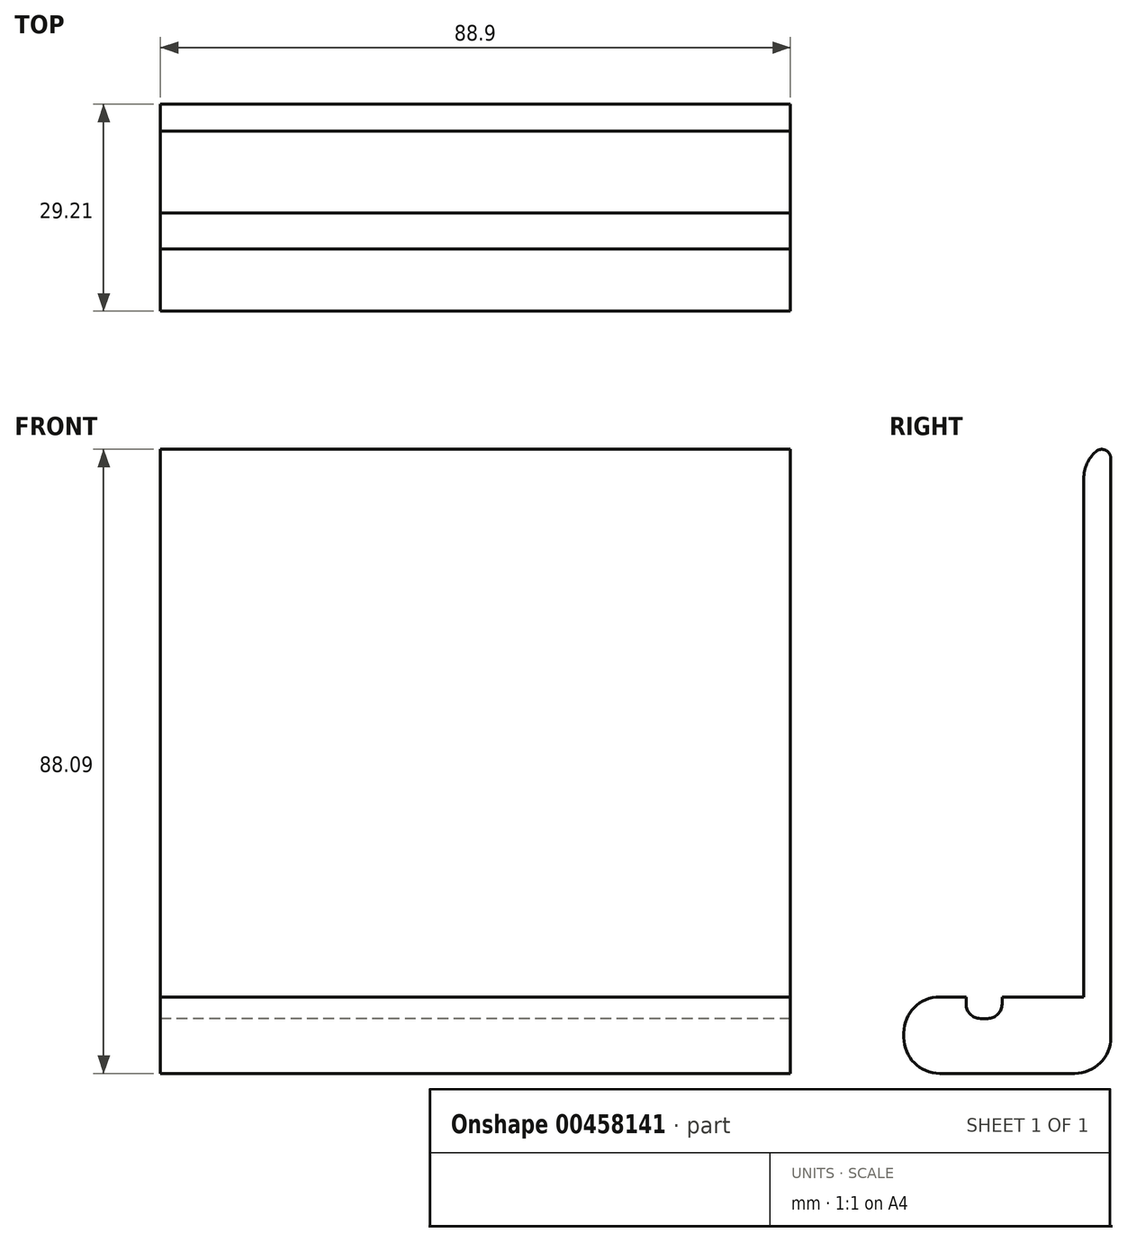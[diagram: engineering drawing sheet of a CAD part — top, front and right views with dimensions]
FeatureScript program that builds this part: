
annotation { "Feature Type Name" : "Feature", "Feature Type Description" : "" }
export const myFeature = defineFeature(function(context is Context, id is Id, definition is map)
    precondition{}
    {
        {
            var Q0;
            Q0=qCreatedBy(makeId("Front.planeOp"),FACE);
            var sketch = newSketch(context, id + "F0", { "sketchPlane" : qUnion([Q0])});
            skLineSegment(sketch, "E0", {"start": v(-36.8, -48.23) * mm, "end": v(52.1, -48.23) * mm});
            skLineSegment(sketch, "E1", {"start": v(-36.8, -48.23) * mm, "end": v(-36.8, 66.07) * mm});
            skLineSegment(sketch, "E2", {"start": v(52.1, -48.23) * mm, "end": v(52.1, 66.07) * mm});
            skLineSegment(sketch, "E3", {"start": v(-36.8, -37.43) * mm, "end": v(52.1, -37.43) * mm});
            skLineSegment(sketch, "E4", {"start": v(52.1, 66.07) * mm, "end": v(-36.8, 66.07) * mm});
            skSolve(sketch);
        }
        {
            var Q0;
            {var subQ0=sQuery(id+"F0.wireOp",EDGE,"vnEuTptI-VBLG-qhPj-jRMl-XnknEwSORpZn");Q0=makeQuery(id+"F0.imprint","IMPRINT",FACE,{"disambiguationData":[TD([[makeQuery(id+"F0.imprint","IMPRINT",EDGE,{"derivedFrom":subQ0}),1.0]])]});}
            var Q1;
            {var subQ0=sQuery(id+"F0.wireOp",EDGE,"xnTbnupX-NSSj-kjbL-TlVA-3KyHgeqRF7kW");Q1=makeQuery(id+"F0.imprint","IMPRINT",FACE,{"disambiguationData":[TD([[makeQuery(id+"F0.imprint","IMPRINT",EDGE,{"derivedFrom":subQ0}),1.0]])]});}
            var Q2;
            {var subQ0=sQuery(id+"F0.wireOp",EDGE,"E0");Q2=makeQuery(id+"F0.imprint","IMPRINT",FACE,{"disambiguationData":[TD([[makeQuery(id+"F0.imprint","IMPRINT",EDGE,{"derivedFrom":subQ0}),1.0]])]});}
            extrude(context, id + "F1", {"entities" : qUnion([Q0, Q1, Q2]), "depth" : 25.4 * mm});
        }
        {
            var Q0;
            Q0=makeQuery(id+"F1.opExtrude","CAP_FACE",FACE,{"disambiguationData":[OSD([sQuery(id+"F0.wireOp",EDGE,"E0"),sQuery(id+"F0.wireOp",EDGE,"E1"),sQuery(id+"F0.wireOp",EDGE,"E2"),sQuery(id+"F0.wireOp",EDGE,"E3"),sQuery(id+"F0.wireOp",EDGE,"vnEuTptI-VBLG-qhPj-jRMl-XnknEwSORpZn"),sQuery(id+"F0.wireOp",EDGE,"viRMa2xW-4hFZ-7MDP-RnKP-vlA6uitpIKmY"),sQuery(id+"F0.wireOp",EDGE,"oGRHd3nG-S1z0-GOV4-n9id-25Wt3cjKO3Ad"),sQuery(id+"F0.wireOp",EDGE,"xnTbnupX-NSSj-kjbL-TlVA-3KyHgeqRF7kW"),sQuery(id+"F0.wireOp",EDGE,"exfSPZ2W-s5OQ-4fdM-lUnk-eJvkYlTu80V8"),sQuery(id+"F0.wireOp",EDGE,"R0UsYyMT-6ugX-hD65-TQg0-aU9kdAwwjer6")])],"isStart":true});
            var sketch = newSketch(context, id + "F2", { "sketchPlane" : qUnion([Q0])});
            skLineSegment(sketch, "E5", {"start": v(-52.1, -48.23) * mm, "end": v(36.8, -48.23) * mm});
            skSolve(sketch);
        }
        {
            var Q0;
            Q0=makeQuery(id+"F2.imprint","IMPRINT",FACE,{"disambiguationData":[TD([[makeQuery(id+"F2.imprint","IMPRINT",EDGE,{"derivedFrom":sQuery(id+"F2.wireOp",EDGE,"E5")}),-1.0]])]});
            var sketch = newSketch(context, id + "F3", { "sketchPlane" : qUnion([Q0])});
            skLineSegment(sketch, "E6.0.0", {"start": v(36.8, -48.23) * mm, "end": v(36.8, -37.43) * mm});
            skLineSegment(sketch, "E6.0.1", {"start": v(36.8, -37.43) * mm, "end": v(-52.1, -37.43) * mm});
            skLineSegment(sketch, "E6.0.2", {"start": v(-52.1, -37.43) * mm, "end": v(-52.1, -48.23) * mm});
            skLineSegment(sketch, "E6.0.3", {"start": v(-52.1, -48.23) * mm, "end": v(36.8, -48.23) * mm});
            skLineSegment(sketch, "E7", {"start": v(36.8, 40.67) * mm, "end": v(36.8, -37.43) * mm});
            skLineSegment(sketch, "E8", {"start": v(36.8, 40.67) * mm, "end": v(-52.1, 40.67) * mm});
            skLineSegment(sketch, "E9", {"start": v(-52.1, 40.67) * mm, "end": v(-52.1, -37.43) * mm});
            skSolve(sketch);
        }
        {
            var Q0;
            Q0 = qSketchRegion(id + "F3", true);
            extrude(context, id + "F4", {"entities" : qUnion([Q0]), "operationType" : NewBodyOperationType.ADD, "depth" : 3.8 * mm});
        }
        {
            var Q0;
            Q0=makeQuery(id+"F1.opExtrude","SWEPT_FACE",FACE,{"disambiguationData":[OSD([sQuery(id+"F0.wireOp",EDGE,"E3")])]});
            var sketch = newSketch(context, id + "F5", { "sketchPlane" : qUnion([Q0])});
            skLineSegment(sketch, "E10", {"start": v(-36.8, -11.53) * mm, "end": v(-36.8, -16.61) * mm});
            skLineSegment(sketch, "E11", {"start": v(-36.8, -16.61) * mm, "end": v(52.1, -16.61) * mm});
            skLineSegment(sketch, "E12", {"start": v(52.1, -16.61) * mm, "end": v(52.1, -11.53) * mm});
            skLineSegment(sketch, "E13", {"start": v(52.1, -11.53) * mm, "end": v(-36.8, -11.53) * mm});
            skSolve(sketch);
        }
        {
            var Q0;
            Q0=makeQuery(id+"F5.imprint","IMPRINT",FACE,{"disambiguationData":[TD([[makeQuery(id+"F5.imprint","IMPRINT",EDGE,{"derivedFrom":sQuery(id+"F5.wireOp",EDGE,"E10")}),-1.0]])]});
            extrude(context, id + "F6", {"entities" : qUnion([Q0]), "operationType" : NewBodyOperationType.REMOVE, "oppositeDirection" : true, "depth" : 3.05 * mm});
        }
        {
            var Q0;
            Q0=makeQuery(id+"F4.opExtrude","CAP_EDGE",EDGE,{"disambiguationData":[OSD([sQuery(id+"F3.wireOp",EDGE,"E8")])],"isStart":true});
            var Q1;
            Q1=makeQuery(id+"F1.opExtrude","CAP_EDGE",EDGE,{"disambiguationData":[OSD([sQuery(id+"F0.wireOp",EDGE,"E3")])],"isStart":false});
            var Q2;
            Q2=makeQuery(id+"F1.opExtrude","CAP_EDGE",EDGE,{"disambiguationData":[OSD([sQuery(id+"F0.wireOp",EDGE,"E0")])],"isStart":false});
            var Q3;
            Q3=makeQuery(id+"F4.opExtrude","CAP_EDGE",EDGE,{"disambiguationData":[OSD([sQuery(id+"F3.wireOp",EDGE,"E6.0.3")])],"isStart":false});
            fillet(context, id + "F7", {"entities" : qUnion([Q0, Q1, Q2, Q3]), "radius" : 5.08 * mm, "tangentPropagation" : true, "allowEdgeOverflow" : false});
        }
        {
            var Q0;
            {var subQ0=sQuery(id+"F3.wireOp",EDGE,"E8");Q0=makeQuery(id+"F7.opFillet","BLEND_EDGE",EDGE,{"blendedFrom":[makeQuery(id+"F4.opExtrude","CAP_EDGE",EDGE,{"disambiguationData":[OSD([subQ0])],"isStart":true}),makeQuery(id+"F4.opExtrude","CAP_FACE",FACE,{"disambiguationData":[OSD([sQuery(id+"F3.wireOp",EDGE,"E6.0.0"),sQuery(id+"F3.wireOp",EDGE,"E6.0.2"),sQuery(id+"F3.wireOp",EDGE,"E6.0.3"),sQuery(id+"F3.wireOp",EDGE,"E7"),subQ0,sQuery(id+"F3.wireOp",EDGE,"E9")])],"isStart":false})],"blendedInto":[makeQuery(id+"F4.opExtrude","CAP_FACE",FACE,{"disambiguationData":[OSD([sQuery(id+"F3.wireOp",EDGE,"E6.0.0"),sQuery(id+"F3.wireOp",EDGE,"E6.0.2"),sQuery(id+"F3.wireOp",EDGE,"E6.0.3"),sQuery(id+"F3.wireOp",EDGE,"E7"),subQ0,sQuery(id+"F3.wireOp",EDGE,"E9")])],"isStart":false})]});}
            fillet(context, id + "F8", {"entities" : qUnion([Q0]), "radius" : 1.27 * mm, "tangentPropagation" : true, "allowEdgeOverflow" : false});
        }
        {
            var Q0;
            Q0=makeQuery(id+"F6.boolean.opBoolean","COPY",EDGE,{"derivedFrom":makeQuery(id+"F6.opExtrude","CAP_EDGE",EDGE,{"disambiguationData":[OSD([sQuery(id+"F5.wireOp",EDGE,"E11")])],"isStart":false})});
            var Q1;
            Q1=makeQuery(id+"F6.boolean.opBoolean","COPY",EDGE,{"derivedFrom":makeQuery(id+"F6.opExtrude","CAP_EDGE",EDGE,{"disambiguationData":[OSD([sQuery(id+"F5.wireOp",EDGE,"E13")])],"isStart":false})});
            fillet(context, id + "F9", {"entities" : qUnion([Q0, Q1]), "radius" : 2.03 * mm, "tangentPropagation" : true, "allowEdgeOverflow" : false});
        }
    });
